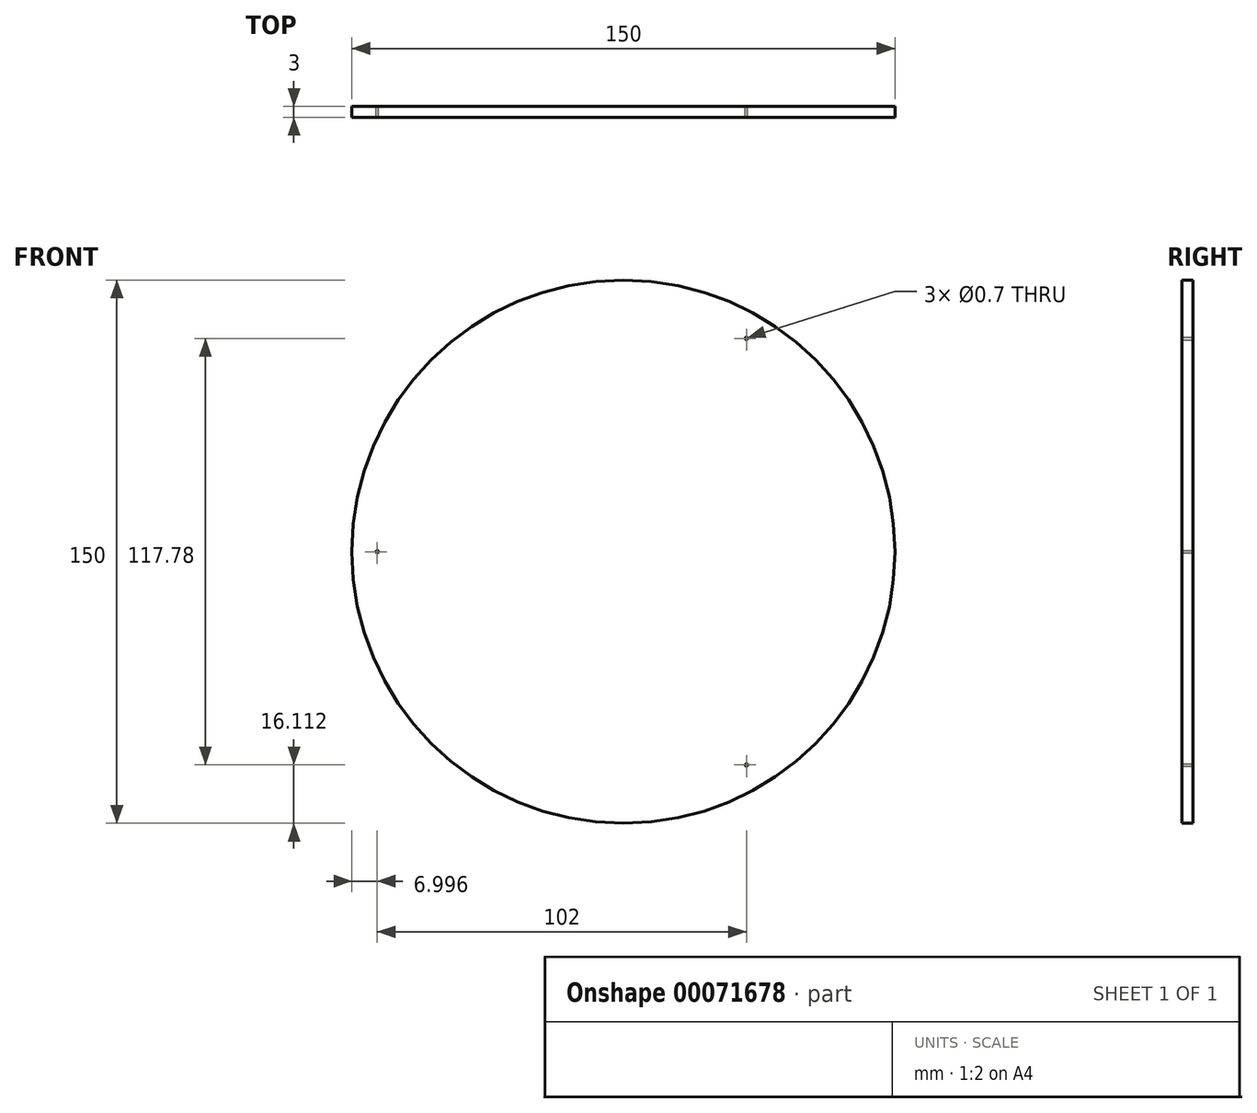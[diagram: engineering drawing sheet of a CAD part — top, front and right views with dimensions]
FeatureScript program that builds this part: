
annotation { "Feature Type Name" : "Feature", "Feature Type Description" : "" }
export const myFeature = defineFeature(function(context is Context, id is Id, definition is map)
    precondition{}
    {
        {
            var Q0;
            Q0=qCreatedBy(makeId("Front.planeOp"),FACE);
            var sketch = newSketch(context, id + "F0", { "sketchPlane" : qUnion([Q0])});
            skCircle(sketch, "E0", {"center": v(-32.77, 12.58) * mm, "radius": 75 * mm});
            skCircle(sketch, "E1", {"center": v(-100.77, 12.58) * mm, "radius": 0.35 * mm});
            skCircle(sketch, "E2.1.0", {"center": v(1.23, -46.3) * mm, "radius": 0.35 * mm});
            skCircle(sketch, "E2.2.0", {"center": v(1.23, 71.47) * mm, "radius": 0.35 * mm});
            skSolve(sketch);
        }
        {
            var Q0;
            Q0=makeQuery(id+"F0.imprint","IMPRINT",FACE,{"disambiguationData":[TD([[makeQuery(id+"F0.imprint","IMPRINT",EDGE,{"derivedFrom":sQuery(id+"F0.wireOp",EDGE,"E0")}),1.0]])]});
            extrude(context, id + "F1", {"entities" : qUnion([Q0]), "depth" : 3 * mm});
        }
    });
